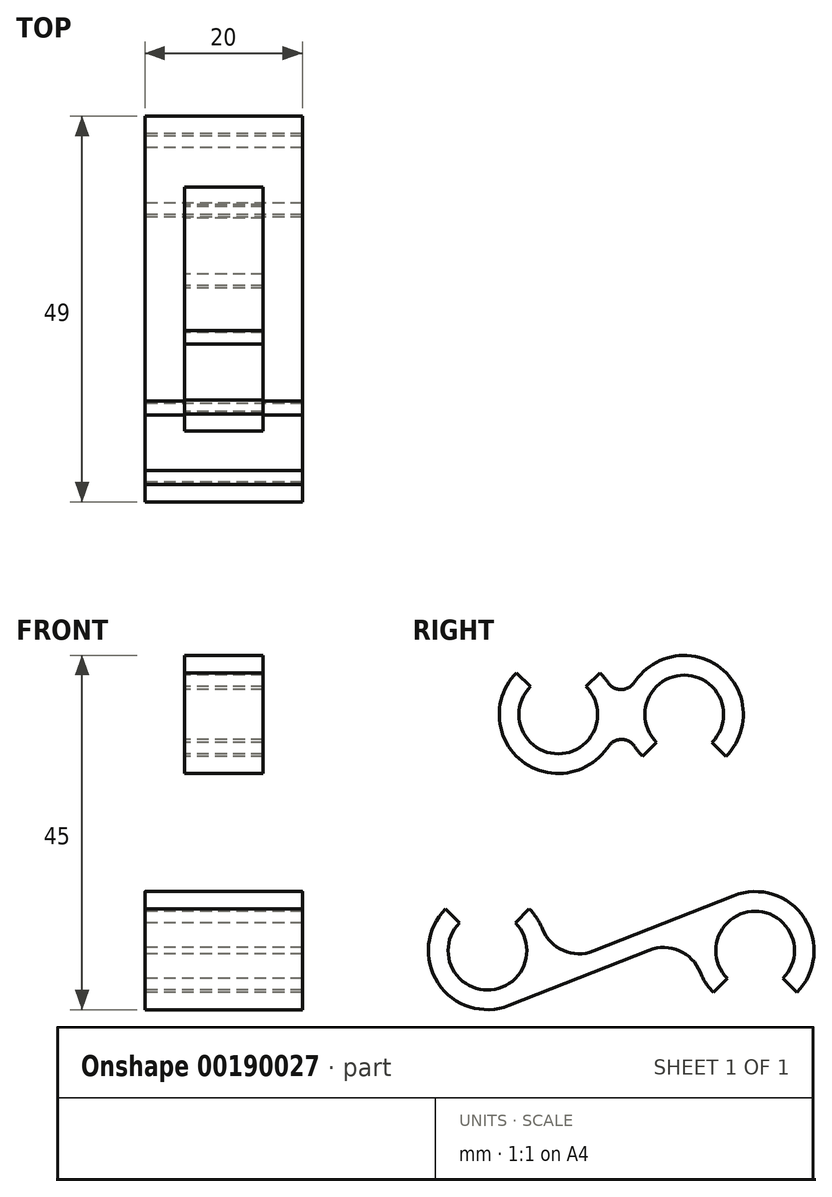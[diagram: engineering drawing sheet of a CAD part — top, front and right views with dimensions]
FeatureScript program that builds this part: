
annotation { "Feature Type Name" : "Feature", "Feature Type Description" : "" }
export const myFeature = defineFeature(function(context is Context, id is Id, definition is map)
    precondition{}
    {
        {
            var Q0;
            Q0=qCreatedBy(makeId("Right.planeOp"),FACE);
            var sketch = newSketch(context, id + "F0", { "sketchPlane" : qUnion([Q0])});
            skArc(sketch, "E0", {"start": v(20.54, -3.54) * mm, "mid": v(17, 5) * mm, "end": v(13.46, -3.54) * mm});
            skArc(sketch, "E1", {"start": v(-20.54, 3.54) * mm, "mid": v(-17, -5) * mm, "end": v(-13.46, 3.54) * mm});
            skArc(sketch, "E2.0", {"start": v(10.03, -2.76) * mm, "mid": v(10.73, -4.12) * mm, "end": v(11.7, -5.3) * mm});
            skArc(sketch, "E3.0", {"start": v(-10.03, 2.76) * mm, "mid": v(-10.73, 4.12) * mm, "end": v(-11.7, 5.3) * mm});
            skLineSegment(sketch, "E4", {"start": v(20.54, -3.54) * mm, "end": v(22.3, -5.3) * mm});
            skLineSegment(sketch, "E5", {"start": v(0, 30) * mm, "end": v(0, -30) * mm, "construction": true});
            skLineSegment(sketch, "E6", {"start": v(-20.54, 3.54) * mm, "end": v(-22.3, 5.3) * mm});
            skLineSegment(sketch, "E7", {"start": v(-13.46, 3.54) * mm, "end": v(-11.7, 5.3) * mm});
            skLineSegment(sketch, "E8", {"start": v(13.46, -3.54) * mm, "end": v(11.7, -5.3) * mm});
            skLineSegment(sketch, "E9", {"start": v(3.54, 0.05) * mm, "end": v(-14.24, -6.97) * mm});
            skLineSegment(sketch, "E10.0", {"start": v(14.24, 6.97) * mm, "end": v(-3.54, -0.05) * mm});
            skArc(sketch, "E11.trimOffspring", {"start": v(22.3, -5.3) * mm, "mid": v(23.27, 4.12) * mm, "end": v(14.24, 6.97) * mm});
            skArc(sketch, "E12.trimOffspring", {"start": v(-22.3, 5.3) * mm, "mid": v(-23.27, -4.12) * mm, "end": v(-14.24, -6.97) * mm});
            skPoint(sketch, "E13.visualSharp", {"position": v(-9.96, -2.6) * mm});
            skArc(sketch, "E13.filletArc", {"start": v(-10.03, 2.76) * mm, "mid": v(-7.36, 0) * mm, "end": v(-3.54, -0.05) * mm});
            skPoint(sketch, "E14.visualSharp", {"position": v(9.96, 2.6) * mm});
            skArc(sketch, "E14.filletArc", {"start": v(10.03, -2.76) * mm, "mid": v(7.36, 0) * mm, "end": v(3.54, 0.05) * mm});
            skArc(sketch, "E15", {"start": v(11.54, 26.46) * mm, "mid": v(8, 35) * mm, "end": v(4.46, 26.46) * mm});
            skArc(sketch, "E16", {"start": v(-11.54, 33.54) * mm, "mid": v(-8, 25) * mm, "end": v(-4.46, 33.54) * mm});
            skArc(sketch, "E17.0", {"start": v(1.7, 25.92) * mm, "mid": v(2.17, 25.28) * mm, "end": v(2.7, 24.7) * mm});
            skArc(sketch, "E18.0", {"start": v(-13.3, 35.3) * mm, "mid": v(-13, 24.41) * mm, "end": v(-2.14, 25.32) * mm});
            skLineSegment(sketch, "E19", {"start": v(11.54, 26.46) * mm, "end": v(13.3, 24.7) * mm});
            skLineSegment(sketch, "E20", {"start": v(4.46, 26.46) * mm, "end": v(2.7, 24.7) * mm});
            skLineSegment(sketch, "E21", {"start": v(-4.46, 33.54) * mm, "end": v(-2.7, 35.3) * mm});
            skLineSegment(sketch, "E22", {"start": v(-11.54, 33.54) * mm, "end": v(-13.3, 35.3) * mm});
            skLineSegment(sketch, "E23", {"start": v(-1.53, 26.08) * mm, "end": v(-2.14, 25.32) * mm});
            skLineSegment(sketch, "E24", {"start": v(1.53, 33.92) * mm, "end": v(2.14, 34.68) * mm});
            skArc(sketch, "E25.trimOffspring", {"start": v(-1.7, 34.08) * mm, "mid": v(-2.17, 34.72) * mm, "end": v(-2.7, 35.3) * mm});
            skArc(sketch, "E26.trimOffspring", {"start": v(13.3, 24.7) * mm, "mid": v(13, 35.59) * mm, "end": v(2.14, 34.68) * mm});
            skPoint(sketch, "E27.visualSharp", {"position": v(-0.6, 31.25) * mm});
            skArc(sketch, "E27.filletArc", {"start": v(-1.7, 34.08) * mm, "mid": v(-0.13, 33.17) * mm, "end": v(1.53, 33.92) * mm});
            skPoint(sketch, "E28.visualSharp", {"position": v(0.6, 28.75) * mm});
            skArc(sketch, "E28.filletArc", {"start": v(1.7, 25.92) * mm, "mid": v(0.13, 26.83) * mm, "end": v(-1.53, 26.08) * mm});
            skSolve(sketch);
        }
        {
            var Q0;
            Q0=makeQuery(id+"F0.imprint","IMPRINT",FACE,{"disambiguationData":[TD([[makeQuery(id+"F0.imprint","IMPRINT",EDGE,{"derivedFrom":sQuery(id+"F0.wireOp",EDGE,"E15")}),-1.0]])]});
            extrude(context, id + "F1", {"entities" : qUnion([Q0]), "endBound" : BoundingType.SYMMETRIC, "depth" : 10 * mm});
        }
        {
            var Q0;
            Q0=makeQuery(id+"F0.imprint","IMPRINT",FACE,{"disambiguationData":[TD([[makeQuery(id+"F0.imprint","IMPRINT",EDGE,{"derivedFrom":sQuery(id+"F0.wireOp",EDGE,"E0")}),-1.0]])]});
            extrude(context, id + "F2", {"entities" : qUnion([Q0]), "endBound" : BoundingType.SYMMETRIC, "depth" : 20 * mm});
        }
    });
